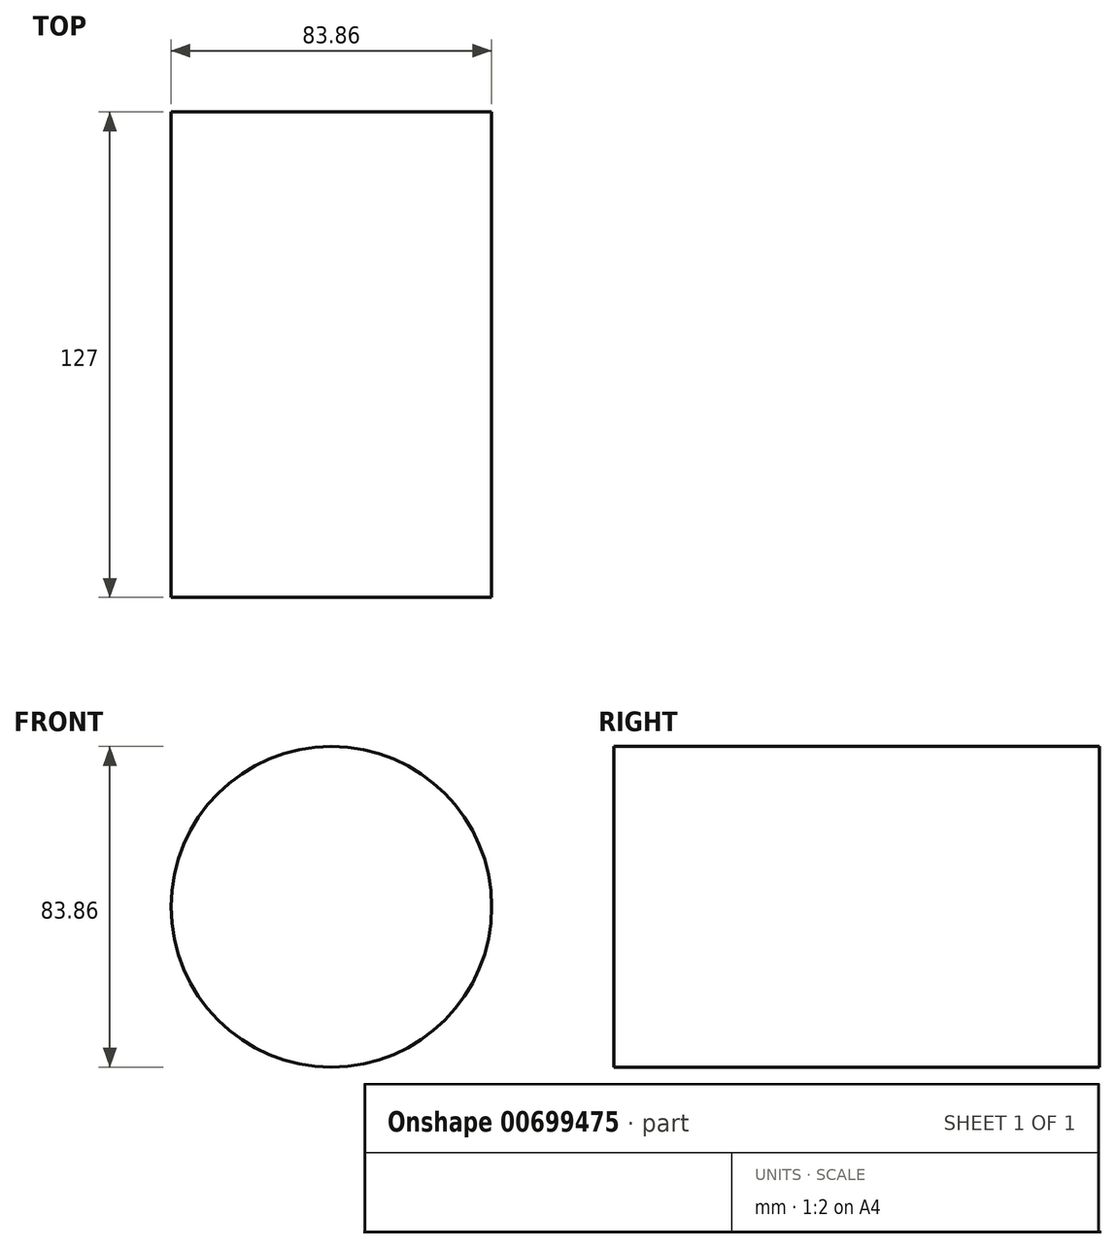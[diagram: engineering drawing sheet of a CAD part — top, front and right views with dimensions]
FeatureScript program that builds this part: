
annotation { "Feature Type Name" : "Feature", "Feature Type Description" : "" }
export const myFeature = defineFeature(function(context is Context, id is Id, definition is map)
    precondition{}
    {
        {
            var Q0;
            Q0=qCreatedBy(makeId("Front.planeOp"),FACE);
            var sketch = newSketch(context, id + "F0", { "sketchPlane" : qUnion([Q0])});
            skCircle(sketch, "E0", {"center": v(0, 0) * mm, "radius": 41.93 * mm});
            skSolve(sketch);
        }
        {
            var Q0;
            Q0=makeQuery(id+"F0.imprint","IMPRINT",FACE,{"disambiguationData":[TD([[makeQuery(id+"F0.imprint","IMPRINT",EDGE,{"derivedFrom":sQuery(id+"F0.wireOp",EDGE,"E0")}),1.0]])]});
            extrude(context, id + "F1", {"entities" : qUnion([Q0]), "oppositeDirection" : true, "depth" : 127 * mm, "offsetDistance" : 25.4 * mm});
        }
    });
